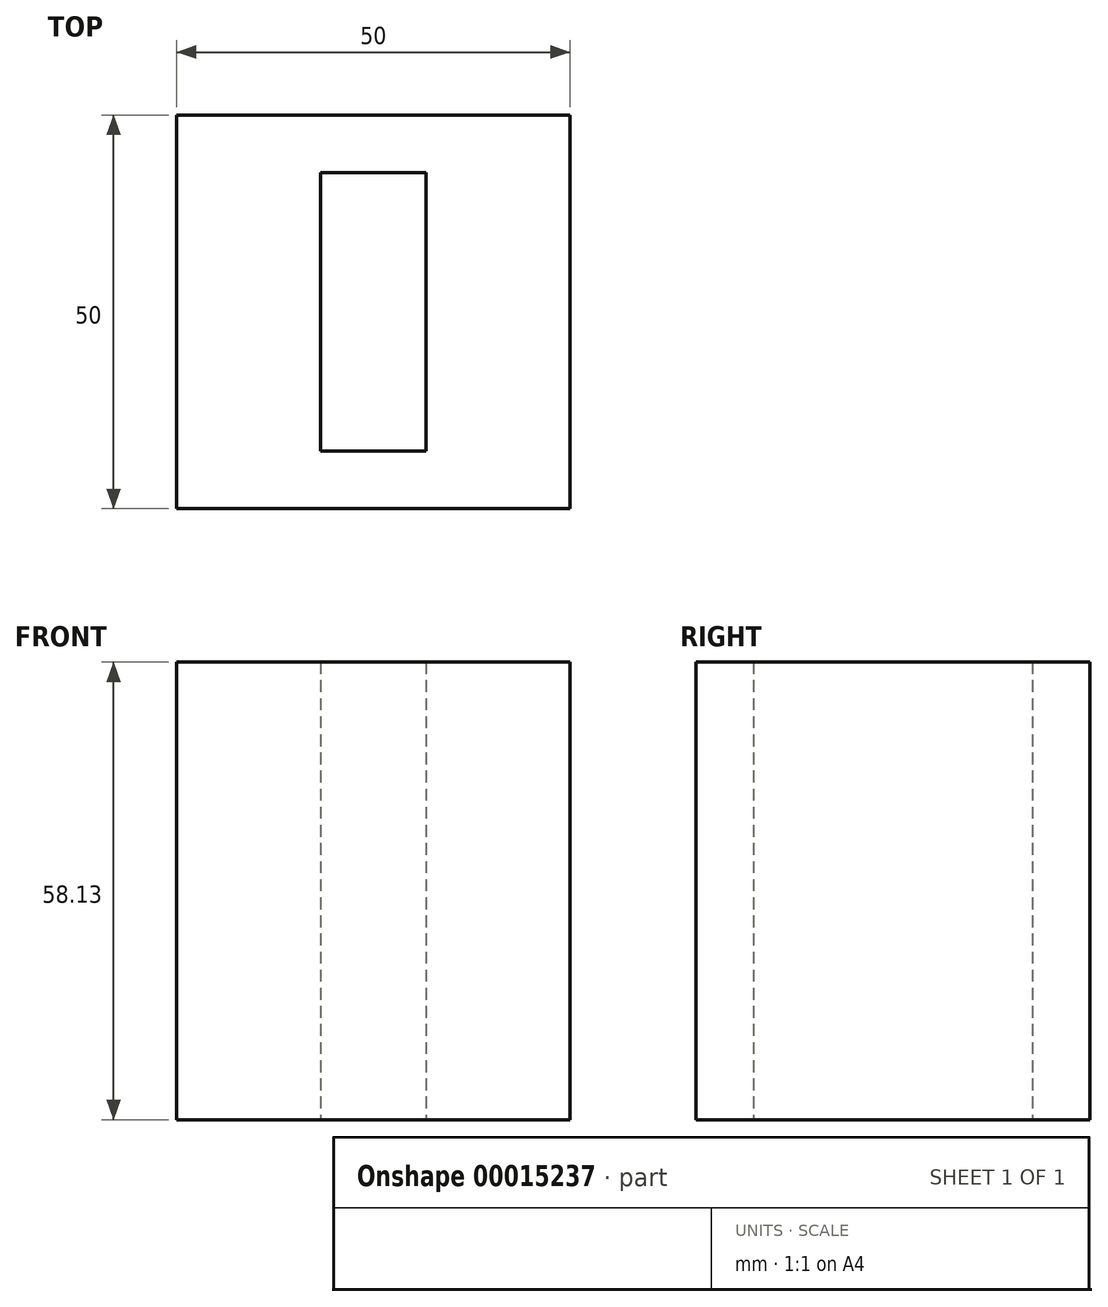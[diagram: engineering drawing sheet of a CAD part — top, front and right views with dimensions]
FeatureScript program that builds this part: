
annotation { "Feature Type Name" : "Feature", "Feature Type Description" : "" }
export const myFeature = defineFeature(function(context is Context, id is Id, definition is map)
    precondition{}
    {
        {
            var Q0;
            Q0=qCreatedBy(makeId("Top.planeOp"),FACE);
            var sketch = newSketch(context, id + "F0", { "sketchPlane" : qUnion([Q0])});
            skLineSegment(sketch, "E0.rect.bottom", {"start": v(25, -25) * mm, "end": v(-25, -25) * mm});
            skLineSegment(sketch, "E0.rect.top", {"start": v(25, 25) * mm, "end": v(-25, 25) * mm});
            skLineSegment(sketch, "E0.rect.left", {"start": v(25, -25) * mm, "end": v(25, 25) * mm});
            skLineSegment(sketch, "E0.rect.right", {"start": v(-25, -25) * mm, "end": v(-25, 25) * mm});
            skPoint(sketch, "E0.rect.middle", {"position": v(0, 0) * mm});
            skSolve(sketch);
        }
        {
            var Q0;
            Q0=qCreatedBy(makeId("Top.planeOp"),FACE);
            var sketch = newSketch(context, id + "F1", { "sketchPlane" : qUnion([Q0])});
            skLineSegment(sketch, "E1.rect.bottom", {"start": v(6.72, -17.7) * mm, "end": v(-6.72, -17.7) * mm});
            skLineSegment(sketch, "E1.rect.top", {"start": v(6.72, 17.7) * mm, "end": v(-6.72, 17.7) * mm});
            skLineSegment(sketch, "E1.rect.left", {"start": v(6.72, -17.7) * mm, "end": v(6.72, 17.7) * mm});
            skLineSegment(sketch, "E1.rect.right", {"start": v(-6.72, -17.7) * mm, "end": v(-6.72, 17.7) * mm});
            skPoint(sketch, "E1.rect.middle", {"position": v(0, 0) * mm});
            skSolve(sketch);
        }
        {
            var Q0;
            Q0=makeQuery(id+"F0.imprint","IMPRINT",FACE,{"disambiguationData":[TD([[makeQuery(id+"F0.imprint","IMPRINT",EDGE,{"derivedFrom":sQuery(id+"F0.wireOp",EDGE,"E0.rect.bottom")}),-1.0]])]});
            var Q1;
            Q1=makeQuery(id+"F1.imprint","IMPRINT",FACE,{"disambiguationData":[TD([[makeQuery(id+"F1.imprint","IMPRINT",EDGE,{"derivedFrom":sQuery(id+"F1.wireOp",EDGE,"E1.rect.bottom")}),-1.0]])]});
            extrude(context, id + "F2", {"entities" : qUnion([Q0, Q1]), "depth" : 58.13 * mm});
        }
    });
